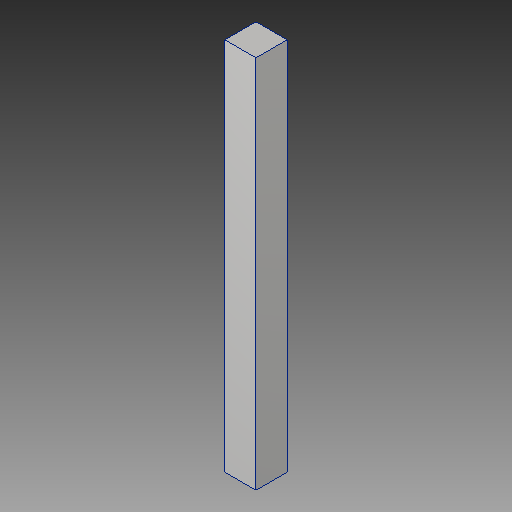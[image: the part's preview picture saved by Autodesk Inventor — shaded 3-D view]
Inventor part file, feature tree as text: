
AUTODESK INVENTOR PART (.ipt)
format: ipt  version: 2017 (Build 210142000, 142)  size: 78,336 bytes
history: native  units: in
note: dims shown in document units (in); Inventor stores cm internally (conversion verified against a paired STEP export)
features: extrude x1, sketch x1
ambient origin geometry x8: Origin, YZ Plane, XZ Plane, XY Plane, X Axis, Y Axis, Z Axis, Center Point
bodies: Solid1 (feature_tree)
feature tree (2):
  extrude  "Extrusion1"  Depth=1.0in
  sketch  "Sketch1"  dims[d0=1.0in d1=1.0in d2=12.0in d3=0.0in]
